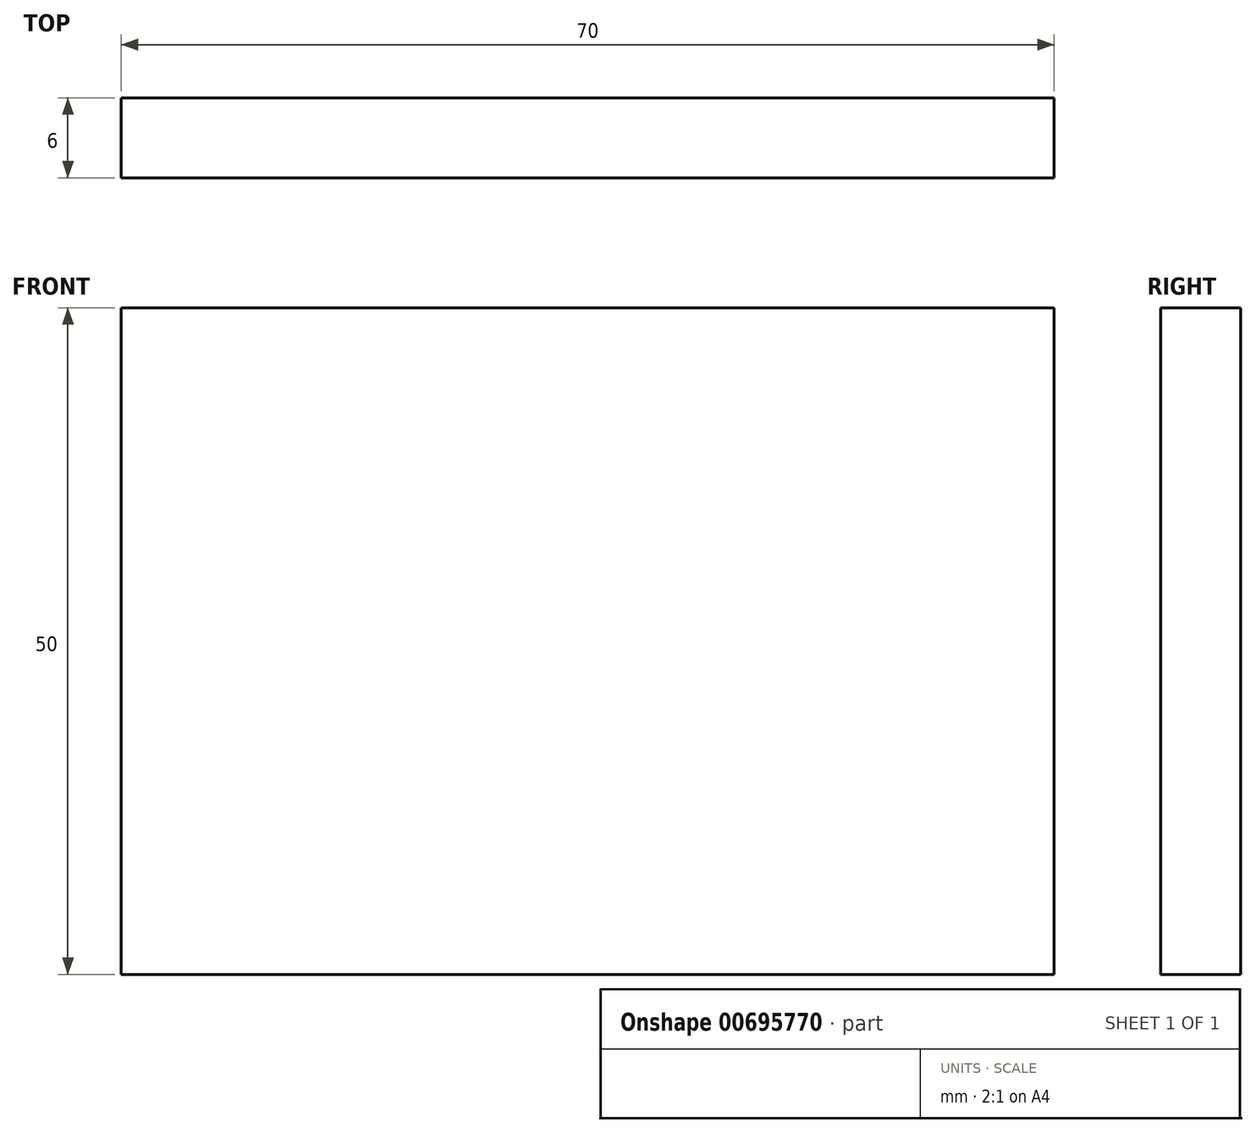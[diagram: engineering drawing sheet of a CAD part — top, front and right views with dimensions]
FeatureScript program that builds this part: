
annotation { "Feature Type Name" : "Feature", "Feature Type Description" : "" }
export const myFeature = defineFeature(function(context is Context, id is Id, definition is map)
    precondition{}
    {
        {
            var Q0;
            Q0=qCreatedBy(makeId("Front.planeOp"),FACE);
            var sketch = newSketch(context, id + "F0", { "sketchPlane" : qUnion([Q0])});
            skLineSegment(sketch, "E0.bottom", {"start": v(0, 0) * mm, "end": v(-70, 0) * mm});
            skLineSegment(sketch, "E0.top", {"start": v(0, 50) * mm, "end": v(-70, 50) * mm});
            skLineSegment(sketch, "E0.left", {"start": v(0, 0) * mm, "end": v(0, 50) * mm});
            skLineSegment(sketch, "E0.right", {"start": v(-70, 0) * mm, "end": v(-70, 50) * mm});
            skSolve(sketch);
        }
        {
            var Q0;
            Q0 = qSketchRegion(id + "F0", true);
            extrude(context, id + "F1", {"entities" : qUnion([Q0]), "oppositeDirection" : true, "depth" : 6 * mm, "offsetDistance" : 25 * mm});
        }
    });
